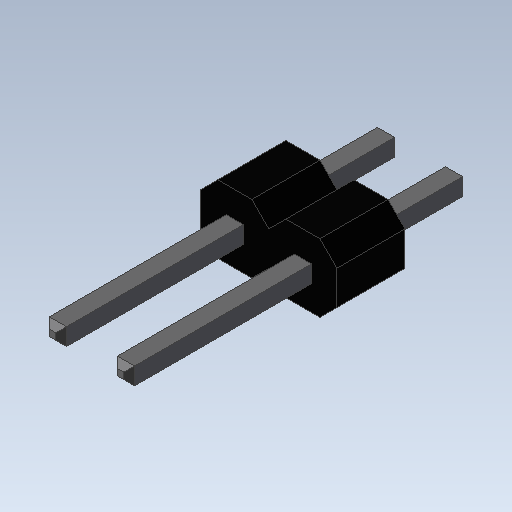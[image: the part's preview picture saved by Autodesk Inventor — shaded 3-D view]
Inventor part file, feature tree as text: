
AUTODESK INVENTOR PART (.ipt)
format: ipt  version: 2020 (Build 240168000, 168)  size: 112,128 bytes
history: imported  units: in
note: dims shown in document units (in); Inventor stores cm internally (conversion verified against a paired STEP export)
features: imported_body x1
ambient origin geometry x8: Origin, YZ Plane, XZ Plane, XY Plane, X Axis, Y Axis, Z Axis, Center Point
bodies: Solid1 (imported_parasolid), Body2 (imported_parasolid)
feature tree (1):
  imported_body  NMx_Import_Brep_tag  [imported B-rep: ~52 faces, bbox_mm=[5.08, 2.54, 12.64]]
